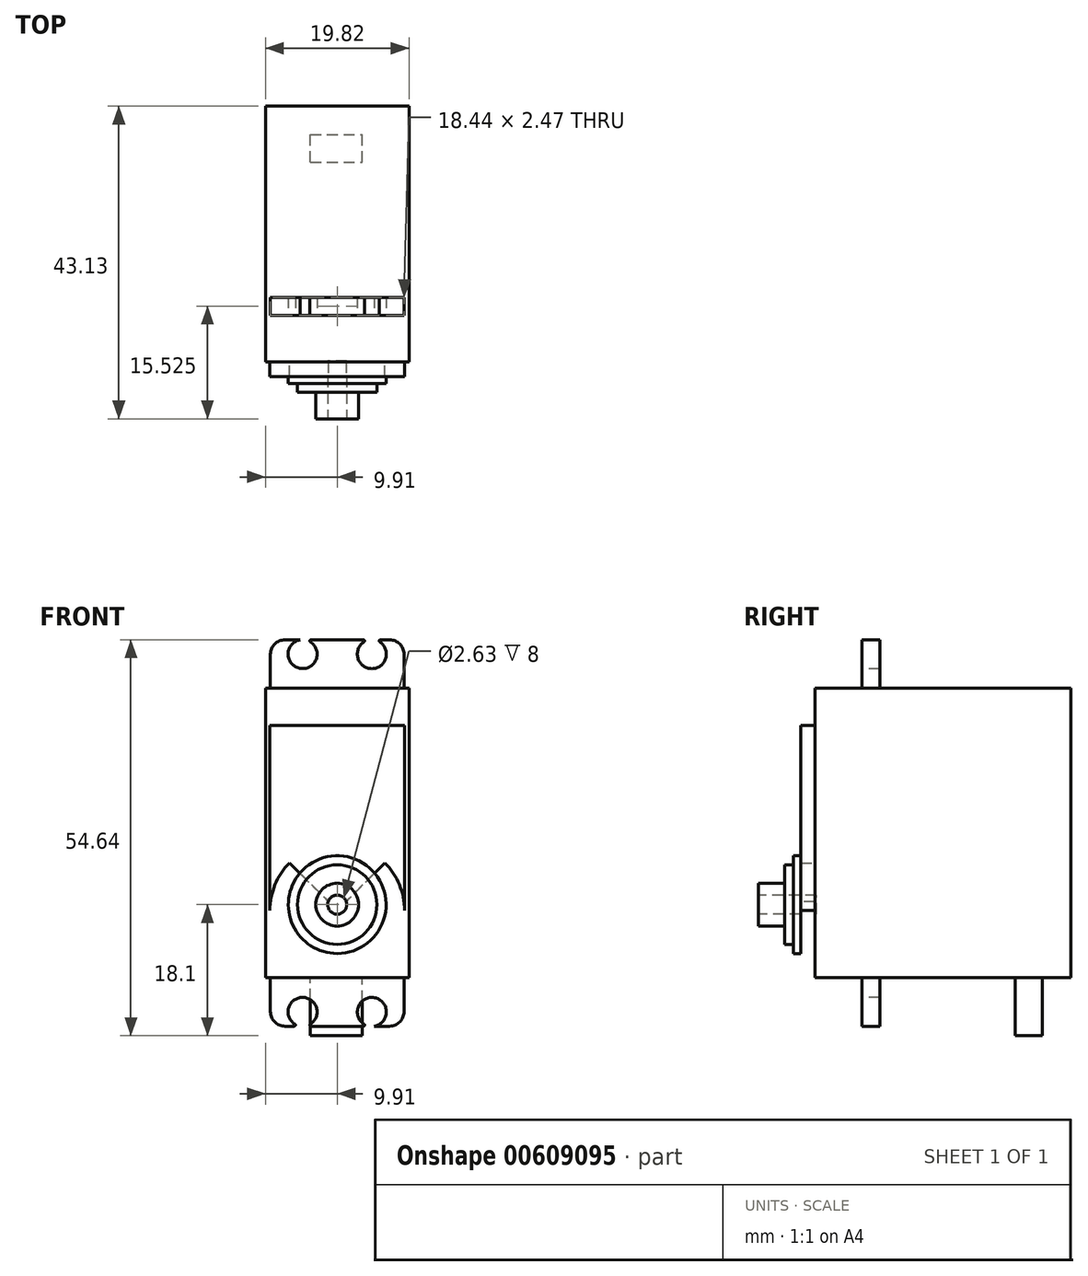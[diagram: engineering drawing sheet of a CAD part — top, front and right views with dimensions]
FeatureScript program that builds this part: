
annotation { "Feature Type Name" : "Feature", "Feature Type Description" : "" }
export const myFeature = defineFeature(function(context is Context, id is Id, definition is map)
    precondition{}
    {
        {
            var Q0;
            Q0=qCreatedBy(makeId("Front.planeOp"),FACE);
            var sketch = newSketch(context, id + "F0", { "sketchPlane" : qUnion([Q0])});
            skLineSegment(sketch, "E0.bottom", {"start": v(-9.9, 19.98) * mm, "end": v(9.9, 19.98) * mm});
            skLineSegment(sketch, "E0.top", {"start": v(-9.9, -19.98) * mm, "end": v(9.9, -19.98) * mm});
            skLineSegment(sketch, "E0.left", {"start": v(-9.9, 19.98) * mm, "end": v(-9.9, -19.98) * mm});
            skLineSegment(sketch, "E0.right", {"start": v(9.9, 19.98) * mm, "end": v(9.9, -19.99) * mm});
            skPoint(sketch, "E0.middle", {"position": v(0, 0) * mm});
            skSolve(sketch);
        }
        {
            var Q0;
            Q0=makeQuery(id+"F0.imprint","IMPRINT",FACE,{"disambiguationData":[TD([[makeQuery(id+"F0.imprint","IMPRINT",EDGE,{"derivedFrom":sQuery(id+"F0.wireOp",EDGE,"E0.bottom")}),-1.0]])]});
            extrude(context, id + "F1", {"entities" : qUnion([Q0]), "depth" : 8.94 * mm, "offsetDistance" : 25 * mm});
        }
        {
            var Q0;
            Q0=makeQuery(id+"F1.opExtrude","SWEPT_FACE",FACE,{"disambiguationData":[OSD([sQuery(id+"F0.wireOp",EDGE,"E0.bottom")])]});
            var sketch = newSketch(context, id + "F2", { "sketchPlane" : qUnion([Q0])});
            skLineSegment(sketch, "E1.bottom", {"start": v(-9.22, 0) * mm, "end": v(9.22, 0) * mm});
            skLineSegment(sketch, "E1.top", {"start": v(-9.22, -2.47) * mm, "end": v(9.22, -2.47) * mm});
            skLineSegment(sketch, "E1.left", {"start": v(-9.22, 0) * mm, "end": v(-9.22, -2.47) * mm});
            skLineSegment(sketch, "E1.right", {"start": v(9.22, 0) * mm, "end": v(9.22, -2.47) * mm});
            skPoint(sketch, "E1.middle", {"position": v(0, -1.23) * mm});
            skSolve(sketch);
        }
        {
            var Q0;
            Q0=makeQuery(id+"F1.opExtrude","SWEPT_FACE",FACE,{"disambiguationData":[OSD([sQuery(id+"F0.wireOp",EDGE,"E0.top")])]});
            var sketch = newSketch(context, id + "F3", { "sketchPlane" : qUnion([Q0])});
            skLineSegment(sketch, "E2.bottom", {"start": v(-9.22, 2.47) * mm, "end": v(9.22, 2.47) * mm});
            skLineSegment(sketch, "E2.top", {"start": v(-9.22, 0) * mm, "end": v(9.22, 0) * mm});
            skLineSegment(sketch, "E2.left", {"start": v(-9.22, 2.47) * mm, "end": v(-9.22, 0) * mm});
            skLineSegment(sketch, "E2.right", {"start": v(9.22, 2.47) * mm, "end": v(9.22, 0) * mm});
            skPoint(sketch, "E2.middle", {"position": v(0, 1.23) * mm});
            skSolve(sketch);
        }
        {
            var Q0;
            Q0=makeQuery(id+"F3.imprint","IMPRINT",FACE,{"disambiguationData":[TD([[makeQuery(id+"F3.imprint","IMPRINT",EDGE,{"derivedFrom":sQuery(id+"F3.wireOp",EDGE,"E2.bottom")}),-1.0]])]});
            extrude(context, id + "F4", {"entities" : qUnion([Q0]), "operationType" : NewBodyOperationType.ADD, "depth" : 6.67 * mm, "offsetDistance" : 25 * mm});
        }
        {
            var Q0;
            Q0=makeQuery(id+"F2.imprint","IMPRINT",FACE,{"disambiguationData":[TD([[makeQuery(id+"F2.imprint","IMPRINT",EDGE,{"derivedFrom":sQuery(id+"F2.wireOp",EDGE,"E1.bottom")}),-1.0]])]});
            extrude(context, id + "F5", {"entities" : qUnion([Q0]), "operationType" : NewBodyOperationType.ADD, "depth" : 6.67 * mm, "offsetDistance" : 25 * mm});
        }
        {
            var Q0;
            Q0=makeQuery(id+"F0.imprint","IMPRINT",FACE,{"disambiguationData":[TD([[makeQuery(id+"F0.imprint","IMPRINT",EDGE,{"derivedFrom":sQuery(id+"F0.wireOp",EDGE,"E0.bottom")}),-1.0]])]});
            extrude(context, id + "F6", {"entities" : qUnion([Q0]), "operationType" : NewBodyOperationType.ADD, "oppositeDirection" : true, "depth" : 20.14 * mm, "offsetDistance" : 25 * mm});
        }
        {
            var Q0;
            Q0=makeQuery(id+"F1.opExtrude","CAP_FACE",FACE,{"disambiguationData":[OSD([sQuery(id+"F0.wireOp",EDGE,"E0.bottom"),sQuery(id+"F0.wireOp",EDGE,"E0.top"),sQuery(id+"F0.wireOp",EDGE,"E0.left"),sQuery(id+"F0.wireOp",EDGE,"E0.right")])],"isStart":false});
            var sketch = newSketch(context, id + "F7", { "sketchPlane" : qUnion([Q0])});
            skLineSegment(sketch, "E3.bottom", {"start": v(-9.3, 14.88) * mm, "end": v(9.3, 14.88) * mm});
            skLineSegment(sketch, "E3.top", {"start": v(-9.3, -19.98) * mm, "end": v(9.3, -19.98) * mm});
            skLineSegment(sketch, "E3.left", {"start": v(-9.3, 14.88) * mm, "end": v(-9.3, -19.98) * mm});
            skLineSegment(sketch, "E3.right", {"start": v(9.3, 14.88) * mm, "end": v(9.3, -19.98) * mm});
            skLineSegment(sketch, "E4.top", {"start": v(-9.3, -1.4) * mm, "end": v(9.3, -1.4) * mm});
            skLineSegment(sketch, "E4.left", {"start": v(-9.3, -19.98) * mm, "end": v(-9.3, -1.4) * mm});
            skLineSegment(sketch, "E4.right", {"start": v(9.3, -19.98) * mm, "end": v(9.3, -1.4) * mm});
            skLineSegment(sketch, "E5", {"start": v(-9.3, -1.4) * mm, "end": v(9.3, -19.98) * mm});
            skLineSegment(sketch, "E6", {"start": v(9.3, -1.4) * mm, "end": v(-9.3, -19.98) * mm});
            skLineSegment(sketch, "E7", {"start": v(0, -10.7) * mm, "end": v(-9.3, -10.7) * mm});
            skLineSegment(sketch, "E8", {"start": v(-9.3, -10.7) * mm, "end": v(0, -10.7) * mm});
            skLineSegment(sketch, "E9", {"start": v(0, -10.7) * mm, "end": v(9.3, -10.7) * mm});
            skLineSegment(sketch, "E10", {"start": v(9.3, -10.7) * mm, "end": v(0, -10.7) * mm});
            skLineSegment(sketch, "E11", {"start": v(0, -10.7) * mm, "end": v(0, -19.98) * mm});
            skLineSegment(sketch, "E12", {"start": v(0, -19.98) * mm, "end": v(0, -10.7) * mm});
            skCircle(sketch, "E13", {"center": v(0, -10.7) * mm, "radius": 9.3 * mm});
            skSolve(sketch);
        }
        {
            var Q0;
            {var subQ1=sQuery(id+"F7.wireOp",EDGE,"E4.top");var subQ3=sQuery(id+"F7.wireOp",EDGE,"E13");var subQ4=makeQuery(id+"F7.imprint","INTERSECT",VERTEX,{"derivedFrom":[subQ1,subQ3]});Q0=makeQuery(id+"F7.imprint","IMPRINT",FACE,{"disambiguationData":[TD([[makeQuery(id+"F7.imprint","IMPRINT",EDGE,{"disambiguationData":[TD([[subQ4,-1.0]])],"derivedFrom":subQ3}),-1.0]])]});}
            var Q1;
            {var subQ1=sQuery(id+"F7.wireOp",EDGE,"E4.top");var subQ3=sQuery(id+"F7.wireOp",EDGE,"E13");var subQ4=makeQuery(id+"F7.imprint","INTERSECT",VERTEX,{"derivedFrom":[subQ1,subQ3]});Q1=makeQuery(id+"F7.imprint","IMPRINT",FACE,{"disambiguationData":[TD([[makeQuery(id+"F7.imprint","IMPRINT",EDGE,{"disambiguationData":[TD([[subQ4,1.0]])],"derivedFrom":subQ3}),-1.0]])]});}
            var Q2;
            {var subQ0=sQuery(id+"F7.wireOp",EDGE,"E6");var subQ3=sQuery(id+"F7.wireOp",EDGE,"E13");var subQ5=makeQuery(id+"F7.imprint","INTERSECT",VERTEX,{"disambiguationData":[OD(0.0)],"derivedFrom":[subQ0,subQ3]});Q2=makeQuery(id+"F7.imprint","IMPRINT",FACE,{"disambiguationData":[TD([[makeQuery(id+"F7.imprint","IMPRINT",EDGE,{"disambiguationData":[TD([[subQ5,1.0]])],"derivedFrom":subQ3}),-1.0]])]});}
            var Q3;
            {var subQ0=sQuery(id+"F7.wireOp",EDGE,"E8");Q3=makeQuery(id+"F7.imprint","IMPRINT",FACE,{"disambiguationData":[TD([[makeQuery(id+"F7.imprint","IMPRINT",EDGE,{"derivedFrom":subQ0}),1.0]])]});}
            var Q4;
            {var subQ0=sQuery(id+"F7.wireOp",EDGE,"E8");Q4=makeQuery(id+"F7.imprint","IMPRINT",FACE,{"disambiguationData":[TD([[makeQuery(id+"F7.imprint","IMPRINT",EDGE,{"derivedFrom":subQ0}),-1.0]])]});}
            var Q5;
            {var subQ0=sQuery(id+"F7.wireOp",EDGE,"E12");Q5=makeQuery(id+"F7.imprint","IMPRINT",FACE,{"disambiguationData":[TD([[makeQuery(id+"F7.imprint","IMPRINT",EDGE,{"derivedFrom":subQ0}),1.0]])]});}
            var Q6;
            {var subQ0=sQuery(id+"F7.wireOp",EDGE,"E12");Q6=makeQuery(id+"F7.imprint","IMPRINT",FACE,{"disambiguationData":[TD([[makeQuery(id+"F7.imprint","IMPRINT",EDGE,{"derivedFrom":subQ0}),-1.0]])]});}
            var Q7;
            {var subQ0=sQuery(id+"F7.wireOp",EDGE,"E10");Q7=makeQuery(id+"F7.imprint","IMPRINT",FACE,{"disambiguationData":[TD([[makeQuery(id+"F7.imprint","IMPRINT",EDGE,{"derivedFrom":subQ0}),1.0]])]});}
            var Q8;
            {var subQ0=sQuery(id+"F7.wireOp",EDGE,"E10");Q8=makeQuery(id+"F7.imprint","IMPRINT",FACE,{"disambiguationData":[TD([[makeQuery(id+"F7.imprint","IMPRINT",EDGE,{"derivedFrom":subQ0}),-1.0]])]});}
            var Q9;
            {var subQ3=sQuery(id+"F7.wireOp",EDGE,"E13");var subQ6=makeQuery(id+"F7.imprint","INTERSECT",VERTEX,{"derivedFrom":[sQuery(id+"F7.wireOp",EDGE,"E4.top"),subQ3]});Q9=makeQuery(id+"F7.imprint","IMPRINT",FACE,{"disambiguationData":[TD([[makeQuery(id+"F7.imprint","IMPRINT",EDGE,{"disambiguationData":[TD([[subQ6,1.0]])],"derivedFrom":subQ3}),1.0]])]});}
            var Q10;
            Q10=makeQuery(id+"F7.imprint","IMPRINT",FACE,{"disambiguationData":[TD([[makeQuery(id+"F7.imprint","IMPRINT",EDGE,{"derivedFrom":sQuery(id+"F7.wireOp",EDGE,"E3.bottom")}),-1.0]])]});
            var Q11;
            {var subQ0=sQuery(id+"F7.wireOp",EDGE,"E5");var subQ3=sQuery(id+"F7.wireOp",EDGE,"E13");var subQ5=makeQuery(id+"F7.imprint","INTERSECT",VERTEX,{"disambiguationData":[OD(0.0)],"derivedFrom":[subQ0,subQ3]});Q11=makeQuery(id+"F7.imprint","IMPRINT",FACE,{"disambiguationData":[TD([[makeQuery(id+"F7.imprint","IMPRINT",EDGE,{"disambiguationData":[TD([[subQ5,-1.0]])],"derivedFrom":subQ3}),-1.0]])]});}
            extrude(context, id + "F8", {"entities" : qUnion([Q0, Q1, Q2, Q3, Q4, Q5, Q6, Q7, Q8, Q9, Q10, Q11]), "operationType" : NewBodyOperationType.ADD, "depth" : 1.98 * mm, "offsetDistance" : 25 * mm});
        }
        {
            var Q0;
            Q0=makeQuery(id+"F8.opExtrude","CAP_FACE",FACE,{"disambiguationData":[OSD([sQuery(id+"F7.wireOp",EDGE,"E3.bottom"),sQuery(id+"F7.wireOp",EDGE,"E3.left"),sQuery(id+"F7.wireOp",EDGE,"E3.right"),sQuery(id+"F7.wireOp",EDGE,"E4.left"),sQuery(id+"F7.wireOp",EDGE,"E4.right"),sQuery(id+"F7.wireOp",EDGE,"E13")])],"isStart":false});
            var sketch = newSketch(context, id + "F9", { "sketchPlane" : qUnion([Q0])});
            skCircle(sketch, "E14", {"center": v(0, -9.88) * mm, "radius": 6.75 * mm});
            skSolve(sketch);
        }
        {
            var Q0;
            Q0=makeQuery(id+"F9.imprint","IMPRINT",FACE,{"disambiguationData":[TD([[makeQuery(id+"F9.imprint","IMPRINT",EDGE,{"derivedFrom":sQuery(id+"F9.wireOp",EDGE,"E14")}),1.0]])]});
            extrude(context, id + "F10", {"entities" : qUnion([Q0]), "operationType" : NewBodyOperationType.ADD, "depth" : 1 * mm, "offsetDistance" : 25 * mm});
        }
        {
            var Q0;
            Q0=makeQuery(id+"F10.opExtrude","CAP_FACE",FACE,{"disambiguationData":[OSD([sQuery(id+"F9.wireOp",EDGE,"E14")])],"isStart":false});
            var sketch = newSketch(context, id + "F11", { "sketchPlane" : qUnion([Q0])});
            skCircle(sketch, "E15", {"center": v(0, -9.88) * mm, "radius": 5.48 * mm});
            skSolve(sketch);
        }
        {
            var Q0;
            Q0=makeQuery(id+"F11.imprint","IMPRINT",FACE,{"disambiguationData":[TD([[makeQuery(id+"F11.imprint","IMPRINT",EDGE,{"derivedFrom":sQuery(id+"F11.wireOp",EDGE,"E15")}),1.0]])]});
            extrude(context, id + "F12", {"entities" : qUnion([Q0]), "operationType" : NewBodyOperationType.ADD, "depth" : 1.2 * mm, "offsetDistance" : 25 * mm});
        }
        {
            var Q0;
            Q0=makeQuery(id+"F12.opExtrude","CAP_FACE",FACE,{"disambiguationData":[OSD([sQuery(id+"F11.wireOp",EDGE,"E15")])],"isStart":false});
            var sketch = newSketch(context, id + "F13", { "sketchPlane" : qUnion([Q0])});
            skCircle(sketch, "E16", {"center": v(0, -9.88) * mm, "radius": 2.95 * mm});
            skSolve(sketch);
        }
        {
            var Q0;
            Q0=makeQuery(id+"F13.imprint","IMPRINT",FACE,{"disambiguationData":[TD([[makeQuery(id+"F13.imprint","IMPRINT",EDGE,{"derivedFrom":sQuery(id+"F13.wireOp",EDGE,"E16")}),1.0]])]});
            extrude(context, id + "F14", {"entities" : qUnion([Q0]), "operationType" : NewBodyOperationType.ADD, "depth" : 3.64 * mm, "offsetDistance" : 25 * mm});
        }
        {
            var Q0;
            Q0=makeQuery(id+"F14.opExtrude","CAP_FACE",FACE,{"disambiguationData":[OSD([sQuery(id+"F13.wireOp",EDGE,"E16")])],"isStart":false});
            var sketch = newSketch(context, id + "F15", { "sketchPlane" : qUnion([Q0])});
            skCircle(sketch, "E17", {"center": v(0, -9.88) * mm, "radius": 1.31 * mm});
            skSolve(sketch);
        }
        {
            var Q0;
            Q0=makeQuery(id+"F15.imprint","IMPRINT",FACE,{"disambiguationData":[TD([[makeQuery(id+"F15.imprint","IMPRINT",EDGE,{"derivedFrom":sQuery(id+"F15.wireOp",EDGE,"E17")}),1.0]])]});
            extrude(context, id + "F16", {"entities" : qUnion([Q0]), "operationType" : NewBodyOperationType.REMOVE, "oppositeDirection" : true, "depth" : 8 * mm, "offsetDistance" : 25 * mm});
        }
        {
            var Q0;
            Q0=makeQuery(id+"F6.opExtrude","CAP_FACE",FACE,{"disambiguationData":[OSD([sQuery(id+"F0.wireOp",EDGE,"E0.bottom"),sQuery(id+"F0.wireOp",EDGE,"E0.top"),sQuery(id+"F0.wireOp",EDGE,"E0.left"),sQuery(id+"F0.wireOp",EDGE,"E0.right")])],"isStart":false});
            extrude(context, id + "F17", {"entities" : qUnion([Q0]), "operationType" : NewBodyOperationType.ADD, "depth" : 6.23 * mm, "offsetDistance" : 25 * mm});
        }
        {
            var Q0;
            {var subQ0=sQuery(id+"F0.wireOp",EDGE,"E0.top");Q0=makeQuery(id+"F17.boolean.opBoolean","MERGE",FACE,{"derivedFrom":[makeQuery(id+"F6.boolean.opBoolean","MERGE",FACE,{"derivedFrom":[makeQuery(id+"F1.opExtrude","SWEPT_FACE",FACE,{"disambiguationData":[OSD([subQ0])]}),makeQuery(id+"F6.opExtrude","SWEPT_FACE",FACE,{"disambiguationData":[OSD([subQ0])]})]}),makeQuery(id+"F17.opExtrude","SWEPT_FACE",FACE,{"disambiguationData":[OSD([subQ0])]})]});}
            var sketch = newSketch(context, id + "F18", { "sketchPlane" : qUnion([Q0])});
            skLineSegment(sketch, "E18.bottom", {"start": v(-3.72, -18.65) * mm, "end": v(3.43, -18.65) * mm});
            skLineSegment(sketch, "E18.top", {"start": v(-3.72, -22.45) * mm, "end": v(3.43, -22.45) * mm});
            skLineSegment(sketch, "E18.left", {"start": v(-3.72, -18.65) * mm, "end": v(-3.72, -22.45) * mm});
            skLineSegment(sketch, "E18.right", {"start": v(3.43, -18.65) * mm, "end": v(3.43, -22.45) * mm});
            skSolve(sketch);
        }
        {
            var Q0;
            Q0=makeQuery(id+"F18.imprint","IMPRINT",FACE,{"disambiguationData":[TD([[makeQuery(id+"F18.imprint","IMPRINT",EDGE,{"derivedFrom":sQuery(id+"F18.wireOp",EDGE,"E18.bottom")}),-1.0]])]});
            extrude(context, id + "F19", {"entities" : qUnion([Q0]), "operationType" : NewBodyOperationType.ADD, "depth" : 8 * mm, "offsetDistance" : 25 * mm});
        }
        {
            var Q0;
            Q0=makeQuery(id+"F5.opExtrude","SWEPT_FACE",FACE,{"disambiguationData":[OSD([sQuery(id+"F2.wireOp",EDGE,"E1.top")])]});
            var sketch = newSketch(context, id + "F20", { "sketchPlane" : qUnion([Q0])});
            skCircle(sketch, "E19", {"center": v(-4.78, 24.68) * mm, "radius": 2 * mm});
            skCircle(sketch, "E20", {"center": v(4.78, 24.68) * mm, "radius": 2 * mm});
            skSolve(sketch);
        }
        {
            var Q0;
            Q0=makeQuery(id+"F4.opExtrude","SWEPT_FACE",FACE,{"disambiguationData":[OSD([sQuery(id+"F3.wireOp",EDGE,"E2.bottom")])]});
            var sketch = newSketch(context, id + "F21", { "sketchPlane" : qUnion([Q0])});
            skCircle(sketch, "E21", {"center": v(-4.78, -24.68) * mm, "radius": 2 * mm});
            skCircle(sketch, "E22", {"center": v(4.78, -24.68) * mm, "radius": 2 * mm});
            skSolve(sketch);
        }
        {
            var Q0;
            {var subQ0=sQuery(id+"F20.wireOp",EDGE,"E20");var subQ1=makeQuery(id+"F5.opExtrude","CAP_EDGE",EDGE,{"disambiguationData":[OSD([sQuery(id+"F2.wireOp",EDGE,"E1.top")])],"isStart":false});var subQ2=makeQuery(id+"F20.imprint","INTERSECT",VERTEX,{"disambiguationData":[OD(0.0)],"derivedFrom":[subQ1,subQ0]});Q0=makeQuery(id+"F20.imprint","IMPRINT",FACE,{"disambiguationData":[TD([[makeQuery(id+"F20.imprint","IMPRINT",EDGE,{"disambiguationData":[TD([[subQ2,1.0]])],"derivedFrom":subQ0}),1.0]])]});}
            var Q1;
            {var subQ0=sQuery(id+"F20.wireOp",EDGE,"E19");var subQ1=makeQuery(id+"F5.opExtrude","CAP_EDGE",EDGE,{"disambiguationData":[OSD([sQuery(id+"F2.wireOp",EDGE,"E1.top")])],"isStart":false});var subQ2=makeQuery(id+"F20.imprint","INTERSECT",VERTEX,{"disambiguationData":[OD(0.0)],"derivedFrom":[subQ1,subQ0]});Q1=makeQuery(id+"F20.imprint","IMPRINT",FACE,{"disambiguationData":[TD([[makeQuery(id+"F20.imprint","IMPRINT",EDGE,{"disambiguationData":[TD([[subQ2,-1.0]])],"derivedFrom":subQ0}),1.0]])]});}
            var Q2;
            {var subQ0=sQuery(id+"F21.wireOp",EDGE,"E22");var subQ1=makeQuery(id+"F4.opExtrude","CAP_EDGE",EDGE,{"disambiguationData":[OSD([sQuery(id+"F3.wireOp",EDGE,"E2.bottom")])],"isStart":false});var subQ2=makeQuery(id+"F21.imprint","INTERSECT",VERTEX,{"disambiguationData":[OD(0.0)],"derivedFrom":[subQ1,subQ0]});Q2=makeQuery(id+"F21.imprint","IMPRINT",FACE,{"disambiguationData":[TD([[makeQuery(id+"F21.imprint","IMPRINT",EDGE,{"disambiguationData":[TD([[subQ2,-1.0]])],"derivedFrom":subQ0}),1.0]])]});}
            var Q3;
            {var subQ0=sQuery(id+"F21.wireOp",EDGE,"E21");var subQ1=makeQuery(id+"F4.opExtrude","CAP_EDGE",EDGE,{"disambiguationData":[OSD([sQuery(id+"F3.wireOp",EDGE,"E2.bottom")])],"isStart":false});var subQ2=makeQuery(id+"F21.imprint","INTERSECT",VERTEX,{"disambiguationData":[OD(0.0)],"derivedFrom":[subQ1,subQ0]});Q3=makeQuery(id+"F21.imprint","IMPRINT",FACE,{"disambiguationData":[TD([[makeQuery(id+"F21.imprint","IMPRINT",EDGE,{"disambiguationData":[TD([[subQ2,1.0]])],"derivedFrom":subQ0}),1.0]])]});}
            extrude(context, id + "F22", {"entities" : qUnion([Q0, Q1, Q2, Q3]), "operationType" : NewBodyOperationType.REMOVE, "oppositeDirection" : true, "depth" : 5 * mm, "offsetDistance" : 25 * mm});
        }
        {
            var Q0;
            {var subQ0=sQuery(id+"F21.wireOp",EDGE,"E21");var subQ1=sQuery(id+"F3.wireOp",EDGE,"E2.bottom");Q0=makeQuery(id+"F22.boolean.opBoolean","COPY",EDGE,{"derivedFrom":makeQuery(id+"F22.opExtrude","SWEPT_EDGE",EDGE,{"disambiguationData":[OSD([subQ1,subQ0]),TDD([makeQuery(id+"F21.imprint","INTERSECT",VERTEX,{"disambiguationData":[OD(0.0)],"derivedFrom":[makeQuery(id+"F4.opExtrude","CAP_EDGE",EDGE,{"disambiguationData":[OSD([subQ1])],"isStart":false}),subQ0]})])]})});}
            var Q1;
            {var subQ0=sQuery(id+"F21.wireOp",EDGE,"E21");var subQ1=sQuery(id+"F3.wireOp",EDGE,"E2.bottom");Q1=makeQuery(id+"F22.boolean.opBoolean","COPY",EDGE,{"derivedFrom":makeQuery(id+"F22.opExtrude","SWEPT_EDGE",EDGE,{"disambiguationData":[OSD([subQ1,subQ0]),TDD([makeQuery(id+"F21.imprint","INTERSECT",VERTEX,{"disambiguationData":[OD(1.0)],"derivedFrom":[makeQuery(id+"F4.opExtrude","CAP_EDGE",EDGE,{"disambiguationData":[OSD([subQ1])],"isStart":false}),subQ0]})])]})});}
            var Q2;
            {var subQ0=sQuery(id+"F21.wireOp",EDGE,"E22");var subQ1=sQuery(id+"F3.wireOp",EDGE,"E2.bottom");Q2=makeQuery(id+"F22.boolean.opBoolean","COPY",EDGE,{"derivedFrom":makeQuery(id+"F22.opExtrude","SWEPT_EDGE",EDGE,{"disambiguationData":[OSD([subQ1,subQ0]),TDD([makeQuery(id+"F21.imprint","INTERSECT",VERTEX,{"disambiguationData":[OD(1.0)],"derivedFrom":[makeQuery(id+"F4.opExtrude","CAP_EDGE",EDGE,{"disambiguationData":[OSD([subQ1])],"isStart":false}),subQ0]})])]})});}
            var Q3;
            {var subQ0=sQuery(id+"F21.wireOp",EDGE,"E22");var subQ1=sQuery(id+"F3.wireOp",EDGE,"E2.bottom");Q3=makeQuery(id+"F22.boolean.opBoolean","COPY",EDGE,{"derivedFrom":makeQuery(id+"F22.opExtrude","SWEPT_EDGE",EDGE,{"disambiguationData":[OSD([subQ1,subQ0]),TDD([makeQuery(id+"F21.imprint","INTERSECT",VERTEX,{"disambiguationData":[OD(0.0)],"derivedFrom":[makeQuery(id+"F4.opExtrude","CAP_EDGE",EDGE,{"disambiguationData":[OSD([subQ1])],"isStart":false}),subQ0]})])]})});}
            var Q4;
            {var subQ0=sQuery(id+"F20.wireOp",EDGE,"E20");var subQ1=sQuery(id+"F2.wireOp",EDGE,"E1.top");Q4=makeQuery(id+"F22.boolean.opBoolean","COPY",EDGE,{"derivedFrom":makeQuery(id+"F22.opExtrude","SWEPT_EDGE",EDGE,{"disambiguationData":[OSD([subQ1,subQ0]),TDD([makeQuery(id+"F20.imprint","INTERSECT",VERTEX,{"disambiguationData":[OD(0.0)],"derivedFrom":[makeQuery(id+"F5.opExtrude","CAP_EDGE",EDGE,{"disambiguationData":[OSD([subQ1])],"isStart":false}),subQ0]})])]})});}
            var Q5;
            {var subQ0=sQuery(id+"F20.wireOp",EDGE,"E19");var subQ1=sQuery(id+"F2.wireOp",EDGE,"E1.top");Q5=makeQuery(id+"F22.boolean.opBoolean","COPY",EDGE,{"derivedFrom":makeQuery(id+"F22.opExtrude","SWEPT_EDGE",EDGE,{"disambiguationData":[OSD([subQ1,subQ0]),TDD([makeQuery(id+"F20.imprint","INTERSECT",VERTEX,{"disambiguationData":[OD(1.0)],"derivedFrom":[makeQuery(id+"F5.opExtrude","CAP_EDGE",EDGE,{"disambiguationData":[OSD([subQ1])],"isStart":false}),subQ0]})])]})});}
            var Q6;
            {var subQ0=sQuery(id+"F20.wireOp",EDGE,"E19");var subQ1=sQuery(id+"F2.wireOp",EDGE,"E1.top");Q6=makeQuery(id+"F22.boolean.opBoolean","COPY",EDGE,{"derivedFrom":makeQuery(id+"F22.opExtrude","SWEPT_EDGE",EDGE,{"disambiguationData":[OSD([subQ1,subQ0]),TDD([makeQuery(id+"F20.imprint","INTERSECT",VERTEX,{"disambiguationData":[OD(0.0)],"derivedFrom":[makeQuery(id+"F5.opExtrude","CAP_EDGE",EDGE,{"disambiguationData":[OSD([subQ1])],"isStart":false}),subQ0]})])]})});}
            var Q7;
            {var subQ0=sQuery(id+"F20.wireOp",EDGE,"E20");var subQ1=sQuery(id+"F2.wireOp",EDGE,"E1.top");Q7=makeQuery(id+"F22.boolean.opBoolean","COPY",EDGE,{"derivedFrom":makeQuery(id+"F22.opExtrude","SWEPT_EDGE",EDGE,{"disambiguationData":[OSD([subQ1,subQ0]),TDD([makeQuery(id+"F20.imprint","INTERSECT",VERTEX,{"disambiguationData":[OD(1.0)],"derivedFrom":[makeQuery(id+"F5.opExtrude","CAP_EDGE",EDGE,{"disambiguationData":[OSD([subQ1])],"isStart":false}),subQ0]})])]})});}
            fillet(context, id + "F23", {"entities" : qUnion([Q0, Q1, Q2, Q3, Q4, Q5, Q6, Q7]), "radius" : .15 * mm, "tangentPropagation" : true, "allowEdgeOverflow" : false});
        }
        {
            var Q0;
            Q0=makeQuery(id+"F5.opExtrude","CAP_EDGE",EDGE,{"disambiguationData":[OSD([sQuery(id+"F2.wireOp",EDGE,"E1.right")])],"isStart":false});
            var Q1;
            Q1=makeQuery(id+"F5.opExtrude","CAP_EDGE",EDGE,{"disambiguationData":[OSD([sQuery(id+"F2.wireOp",EDGE,"E1.left")])],"isStart":false});
            var Q2;
            Q2=makeQuery(id+"F4.opExtrude","CAP_EDGE",EDGE,{"disambiguationData":[OSD([sQuery(id+"F3.wireOp",EDGE,"E2.left")])],"isStart":false});
            var Q3;
            Q3=makeQuery(id+"F4.opExtrude","CAP_EDGE",EDGE,{"disambiguationData":[OSD([sQuery(id+"F3.wireOp",EDGE,"E2.right")])],"isStart":false});
            fillet(context, id + "F24", {"entities" : qUnion([Q0, Q1, Q2, Q3]), "radius" : 2 * mm, "tangentPropagation" : true, "allowEdgeOverflow" : false});
        }
    });
